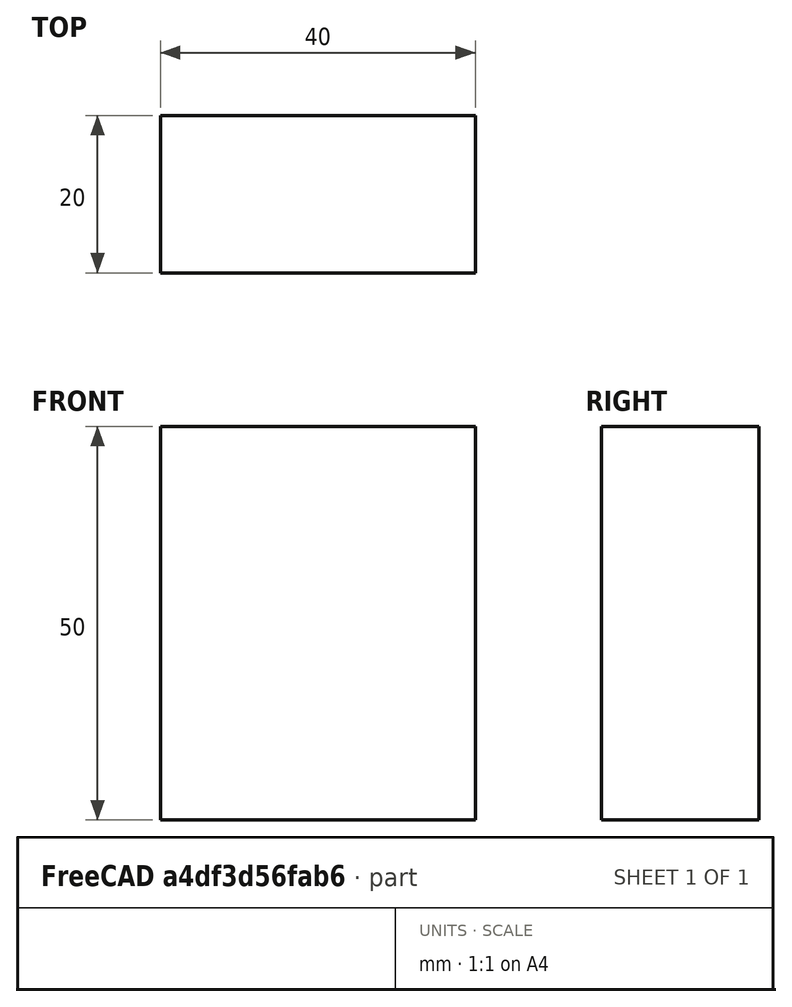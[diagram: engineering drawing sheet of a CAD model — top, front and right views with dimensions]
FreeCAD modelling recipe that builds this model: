
FCSTD DOCUMENT  (FreeCAD 0.15R4671 (Git))
Label: Flat Bar 40x20 EN10058 S235JR
License: All rights reserved
LicenseURL: http://en.wikipedia.org/wiki/All_rights_reserved
objects: Sketcher::SketchObject×1, Part::Extrusion×1
note: 2 computed .brp shape members not serialized (recipe doc carries the construction recipe); baked Part::Feature solids carry a one-line shape summary decoded from their .brp

FEATURE [Sketcher::SketchObject] Sketch
  sketch-geometry (4):
    g0: LineSegment StartX=-20 StartY=-10 StartZ=0 EndX=20 EndY=-10 EndZ=0
    g1: LineSegment StartX=20 StartY=-10 StartZ=0 EndX=20 EndY=10 EndZ=0
    g2: LineSegment StartX=20 StartY=10 StartZ=0 EndX=-20 EndY=10 EndZ=0
    g3: LineSegment StartX=-20 StartY=10 StartZ=0 EndX=-20 EndY=-10 EndZ=0
  constraints (12):
    c: Coincident(g0,g1)
    c: Coincident(g1,g2)
    c: Coincident(g2,g3)
    c: Coincident(g3,g0)
    c: Horizontal(g0)
    c: Horizontal(g2)
    c: Vertical(g1)
    c: Vertical(g3)
    c: Symmetric(g1,g2,g-2)
    c: Symmetric(g0,g1,g-1)
    c: DistanceY(g1) = 20
    c: DistanceX(g0) = 40
FEATURE [Part::Extrusion] Extrude  label="Flat Bar 40x20 EN10058 S235JR"
  Base = -> Sketch
  Dir = (0,0,50)
  Solid = true
